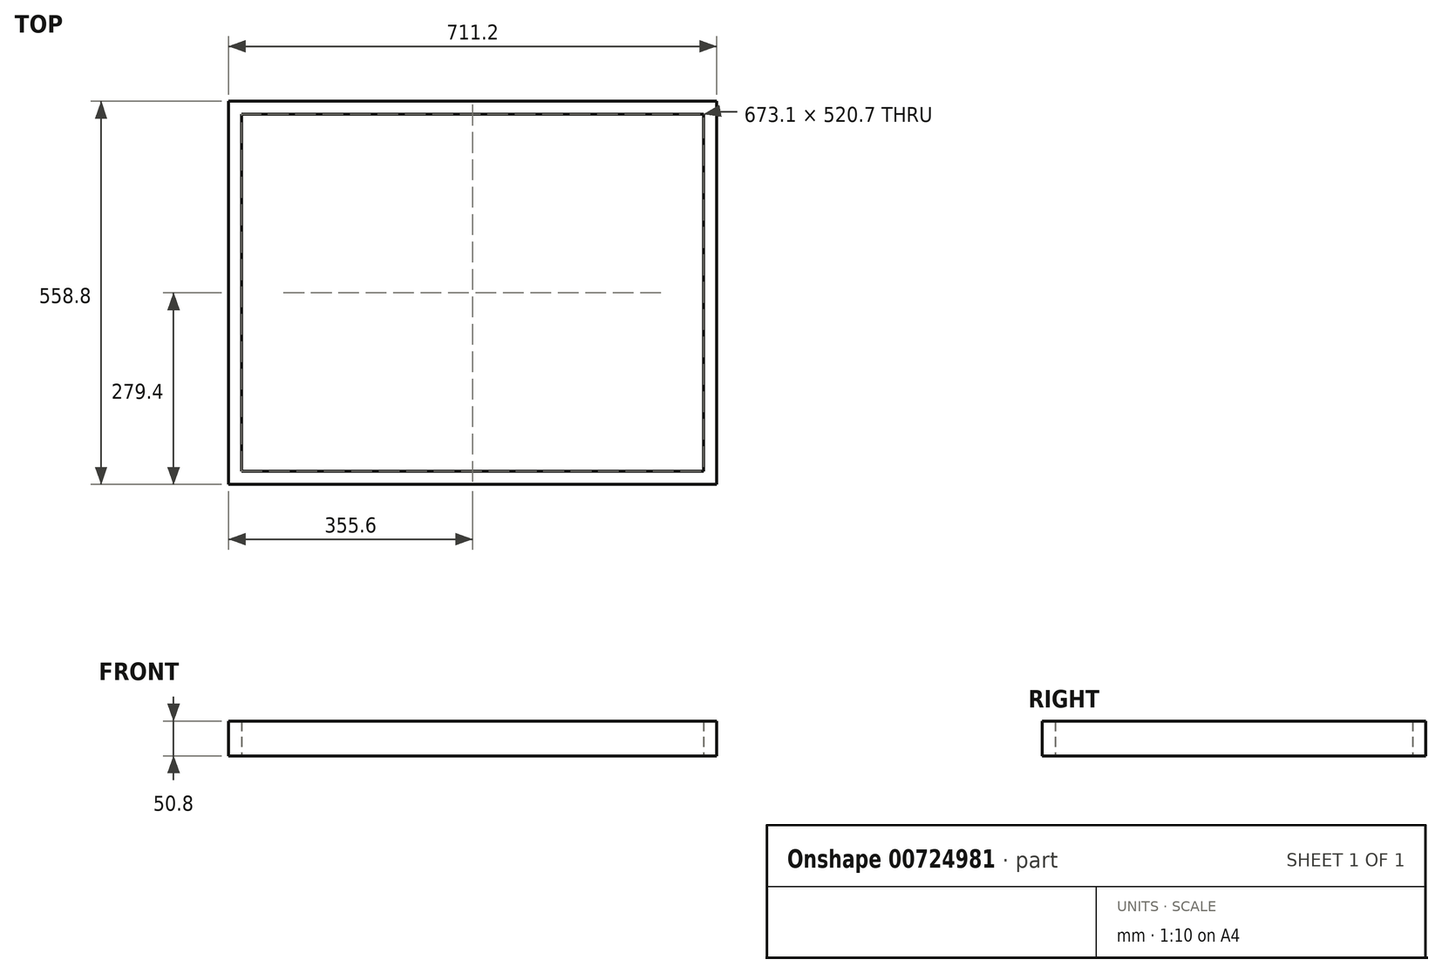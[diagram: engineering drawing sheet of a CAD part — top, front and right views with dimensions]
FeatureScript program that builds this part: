
annotation { "Feature Type Name" : "Feature", "Feature Type Description" : "" }
export const myFeature = defineFeature(function(context is Context, id is Id, definition is map)
    precondition{}
    {
        {
            var Q0;
            Q0=qCreatedBy(makeId("Top.planeOp"),FACE);
            var sketch = newSketch(context, id + "F0", { "sketchPlane" : qUnion([Q0])});
            skLineSegment(sketch, "E0.bottom", {"start": v(355.6, 279.4) * mm, "end": v(-355.6, 279.4) * mm});
            skLineSegment(sketch, "E0.top", {"start": v(355.6, -279.4) * mm, "end": v(-355.6, -279.4) * mm});
            skLineSegment(sketch, "E0.left", {"start": v(355.6, 279.4) * mm, "end": v(355.6, -279.4) * mm});
            skLineSegment(sketch, "E0.right", {"start": v(-355.6, 279.4) * mm, "end": v(-355.6, -279.4) * mm});
            skPoint(sketch, "E0.middle", {"position": v(0, 0) * mm});
            skLineSegment(sketch, "E1.bottom", {"start": v(-336.55, 260.35) * mm, "end": v(336.55, 260.35) * mm});
            skLineSegment(sketch, "E1.top", {"start": v(-336.55, -260.35) * mm, "end": v(336.55, -260.35) * mm});
            skLineSegment(sketch, "E1.left", {"start": v(-336.55, 260.35) * mm, "end": v(-336.55, -260.35) * mm});
            skLineSegment(sketch, "E1.right", {"start": v(336.55, 260.35) * mm, "end": v(336.55, -260.35) * mm});
            skSolve(sketch);
        }
        {
            var Q0;
            Q0=makeQuery(id+"F0.imprint","IMPRINT",FACE,{"disambiguationData":[TD([[makeQuery(id+"F0.imprint","IMPRINT",EDGE,{"derivedFrom":sQuery(id+"F0.wireOp",EDGE,"E0.bottom")}),1.0]])]});
            extrude(context, id + "F1", {"entities" : qUnion([Q0]), "depth" : 50.8 * mm, "offsetDistance" : 25.4 * mm});
        }
    });
